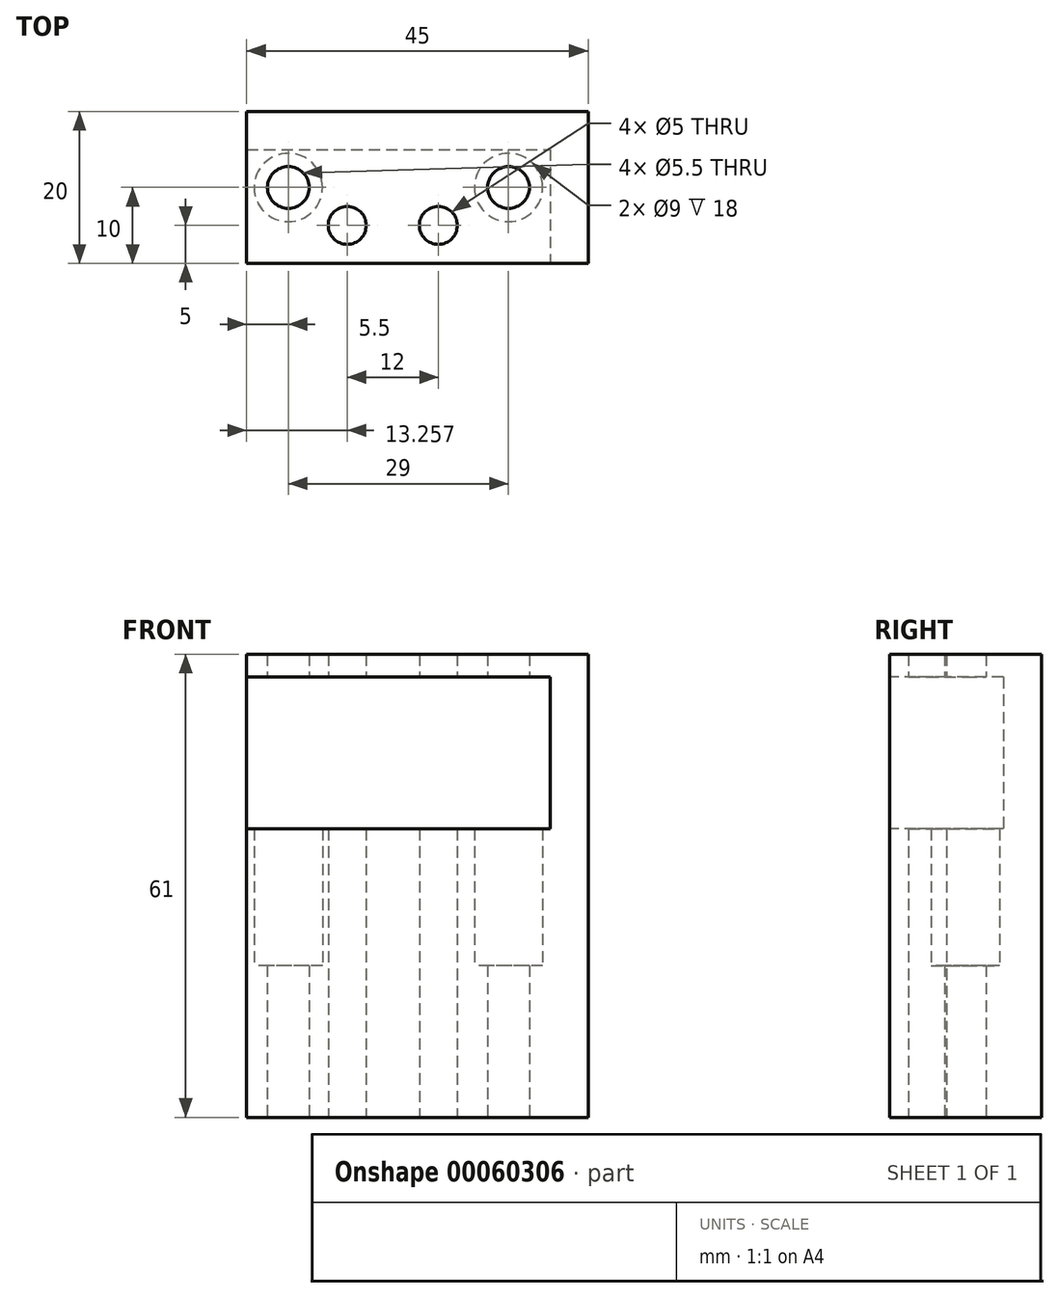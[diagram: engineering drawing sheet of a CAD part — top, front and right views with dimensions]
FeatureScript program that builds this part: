
annotation { "Feature Type Name" : "Feature", "Feature Type Description" : "" }
export const myFeature = defineFeature(function(context is Context, id is Id, definition is map)
    precondition{}
    {
        {
            var Q0;
            Q0=qCreatedBy(makeId("Top.planeOp"),FACE);
            var sketch = newSketch(context, id + "F0", { "sketchPlane" : qUnion([Q0])});
            skLineSegment(sketch, "E0.bottom", {"start": v(-20, 10) * mm, "end": v(20, 10) * mm});
            skLineSegment(sketch, "E0.top", {"start": v(-20, -10) * mm, "end": v(20, -10) * mm});
            skLineSegment(sketch, "E0.left", {"start": v(-20, 10) * mm, "end": v(-20, -10) * mm});
            skLineSegment(sketch, "E0.right", {"start": v(20, 10) * mm, "end": v(20, -10) * mm});
            skLineSegment(sketch, "E1", {"start": v(0, 10) * mm, "end": v(0, -10) * mm, "construction": true});
            skLineSegment(sketch, "E2.bottom", {"start": v(20, 10) * mm, "end": v(25, 10) * mm});
            skLineSegment(sketch, "E2.top", {"start": v(20, -10) * mm, "end": v(25, -10) * mm});
            skLineSegment(sketch, "E2.right", {"start": v(25, 10) * mm, "end": v(25, -10) * mm});
            skLineSegment(sketch, "E3.top", {"start": v(-20, 5) * mm, "end": v(20, 5) * mm});
            skLineSegment(sketch, "E3.left", {"start": v(-20, 10) * mm, "end": v(-20, 5) * mm});
            skLineSegment(sketch, "E3.right", {"start": v(20, 10) * mm, "end": v(20, 5) * mm});
            skCircle(sketch, "E4", {"center": v(-6.74, -5) * mm, "radius": 2.5 * mm});
            skCircle(sketch, "E5", {"center": v(5.26, -5) * mm, "radius": 2.5 * mm});
            skLineSegment(sketch, "E6", {"start": v(25, 0) * mm, "end": v(-20, 0) * mm, "construction": true});
            skCircle(sketch, "E7", {"center": v(14.5, 0) * mm, "radius": 4.5 * mm});
            skCircle(sketch, "E8", {"center": v(-14.5, 0) * mm, "radius": 4.5 * mm});
            skCircle(sketch, "E9", {"center": v(14.5, 0) * mm, "radius": 2.75 * mm});
            skCircle(sketch, "E10", {"center": v(-14.5, 0) * mm, "radius": 2.75 * mm});
            skSolve(sketch);
        }
        {
            var Q0;
            Q0=makeQuery(id+"F0.imprint","IMPRINT",FACE,{"disambiguationData":[TD([[makeQuery(id+"F0.imprint","IMPRINT",EDGE,{"derivedFrom":sQuery(id+"F0.wireOp",EDGE,"E0.top")}),1.0]])]});
            extrude(context, id + "F1", {"entities" : qUnion([Q0]), "depth" : 38 * mm});
        }
        {
            var Q0;
            Q0=makeQuery(id+"F0.imprint","IMPRINT",FACE,{"disambiguationData":[TD([[makeQuery(id+"F0.imprint","IMPRINT",EDGE,{"derivedFrom":sQuery(id+"F0.wireOp",EDGE,"E2.bottom")}),-1.0]])]});
            var Q1;
            Q1=makeQuery(id+"F0.imprint","IMPRINT",FACE,{"disambiguationData":[TD([[makeQuery(id+"F0.imprint","IMPRINT",EDGE,{"derivedFrom":sQuery(id+"F0.wireOp",EDGE,"E0.bottom")}),-1.0]])]});
            extrude(context, id + "F2", {"entities" : qUnion([Q0, Q1]), "operationType" : NewBodyOperationType.ADD, "depth" : 61 * mm});
        }
        {
            var Q0;
            Q0=makeQuery(id+"F0.imprint","IMPRINT",FACE,{"disambiguationData":[TD([[makeQuery(id+"F0.imprint","IMPRINT",EDGE,{"derivedFrom":sQuery(id+"F0.wireOp",EDGE,"E0.top")}),1.0]])]});
            extrude(context, id + "F3", {"entities" : qUnion([Q0]), "operationType" : NewBodyOperationType.ADD, "depth" : 61 * mm, "hasSecondDirection" : true, "secondDirectionOppositeDirection" : false, "secondDirectionDepth" : 58 * mm});
        }
        {
            var Q0;
            Q0=makeQuery(id+"F0.imprint","IMPRINT",FACE,{"disambiguationData":[TD([[makeQuery(id+"F0.imprint","IMPRINT",EDGE,{"derivedFrom":sQuery(id+"F0.wireOp",EDGE,"E8")}),1.0]])]});
            var Q1;
            Q1=makeQuery(id+"F0.imprint","IMPRINT",FACE,{"disambiguationData":[TD([[makeQuery(id+"F0.imprint","IMPRINT",EDGE,{"derivedFrom":sQuery(id+"F0.wireOp",EDGE,"E7")}),1.0]])]});
            extrude(context, id + "F4", {"entities" : qUnion([Q0, Q1]), "operationType" : NewBodyOperationType.ADD, "depth" : 20 * mm});
        }
        {
            var Q0;
            Q0=makeQuery(id+"F0.imprint","IMPRINT",FACE,{"disambiguationData":[TD([[makeQuery(id+"F0.imprint","IMPRINT",EDGE,{"derivedFrom":sQuery(id+"F0.wireOp",EDGE,"E8")}),1.0]])]});
            var Q1;
            Q1=makeQuery(id+"F0.imprint","IMPRINT",FACE,{"disambiguationData":[TD([[makeQuery(id+"F0.imprint","IMPRINT",EDGE,{"derivedFrom":sQuery(id+"F0.wireOp",EDGE,"E7")}),1.0]])]});
            extrude(context, id + "F5", {"entities" : qUnion([Q0, Q1]), "operationType" : NewBodyOperationType.ADD, "depth" : 61 * mm, "hasSecondDirection" : true, "secondDirectionOppositeDirection" : false, "secondDirectionDepth" : 58 * mm});
        }
    });
